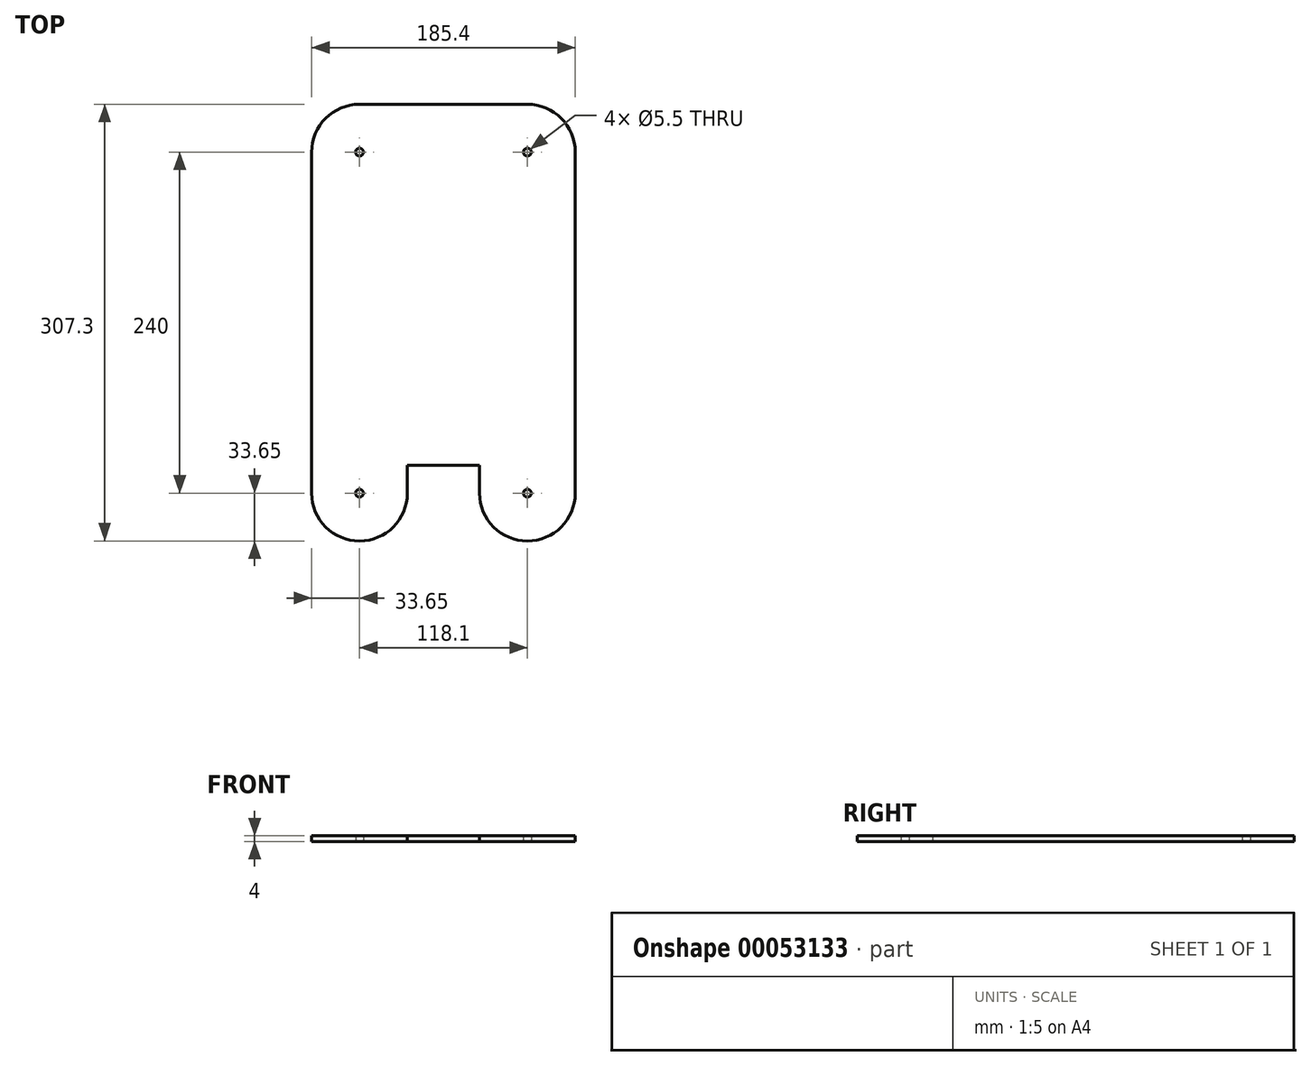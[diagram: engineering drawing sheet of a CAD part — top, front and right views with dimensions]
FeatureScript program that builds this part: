
annotation { "Feature Type Name" : "Feature", "Feature Type Description" : "" }
export const myFeature = defineFeature(function(context is Context, id is Id, definition is map)
    precondition{}
    {
        {
            var Q0;
            Q0=qCreatedBy(makeId("Top.planeOp"),FACE);
            var sketch = newSketch(context, id + "F0", { "sketchPlane" : qUnion([Q0])});
            skLineSegment(sketch, "E0.rect.bottom", {"start": v(61.55, 153.65) * mm, "end": v(-61.55, 153.65) * mm});
            skLineSegment(sketch, "E0.rect.top", {"start": v(61.55, -153.65) * mm, "end": v(-61.55, -153.65) * mm});
            skLineSegment(sketch, "E0.rect.left", {"start": v(92.7, 122.5) * mm, "end": v(92.7, -122.5) * mm});
            skLineSegment(sketch, "E0.rect.right", {"start": v(-92.7, 122.5) * mm, "end": v(-92.7, -122.5) * mm});
            skPoint(sketch, "E0.rect.middle", {"position": v(0, 0) * mm});
            skArc(sketch, "E1", {"start": v(-61.55, 153.65) * mm, "mid": v(-83.58, 144.53) * mm, "end": v(-92.7, 122.5) * mm});
            skPoint(sketch, "E2", {"position": v(-61.55, 153.65) * mm});
            skPoint(sketch, "E3", {"position": v(-92.7, 122.5) * mm});
            skPoint(sketch, "E4", {"position": v(-92.7, 153.65) * mm});
            skPoint(sketch, "E5", {"position": v(92.7, 153.65) * mm});
            skPoint(sketch, "E6", {"position": v(-92.7, -153.65) * mm});
            skPoint(sketch, "E7", {"position": v(92.7, -153.65) * mm});
            skArc(sketch, "E8", {"start": v(92.7, 122.5) * mm, "mid": v(83.58, 144.53) * mm, "end": v(61.55, 153.65) * mm});
            skArc(sketch, "E9", {"start": v(61.55, -153.65) * mm, "mid": v(83.58, -144.53) * mm, "end": v(92.7, -122.5) * mm});
            skArc(sketch, "E10", {"start": v(-92.7, -122.5) * mm, "mid": v(-83.58, -144.53) * mm, "end": v(-61.55, -153.65) * mm});
            skPoint(sketch, "E11", {"position": v(61.55, 153.65) * mm});
            skPoint(sketch, "E12", {"position": v(92.7, 122.5) * mm});
            skPoint(sketch, "E13", {"position": v(92.7, -122.5) * mm});
            skPoint(sketch, "E14", {"position": v(-92.7, -122.5) * mm});
            skPoint(sketch, "E15", {"position": v(61.55, -153.65) * mm});
            skPoint(sketch, "E16", {"position": v(-61.55, -153.65) * mm});
            skPoint(sketch, "E17", {"position": v(-183.97, 39.4) * mm});
            skPoint(sketch, "E18", {"position": v(-61.55, 120) * mm});
            skPoint(sketch, "E19", {"position": v(61.55, 120) * mm});
            skPoint(sketch, "E20", {"position": v(61.55, -120) * mm});
            skPoint(sketch, "E21", {"position": v(-61.55, -120) * mm});
            skPoint(sketch, "E22", {"position": v(59.05, -120) * mm});
            skPoint(sketch, "E23", {"position": v(-59.05, -120) * mm});
            skPoint(sketch, "E24", {"position": v(-59.05, 120) * mm});
            skPoint(sketch, "E25", {"position": v(59.05, 120) * mm});
            skCircle(sketch, "E26", {"center": v(59.05, -120) * mm, "radius": 2.75 * mm});
            skCircle(sketch, "E27", {"center": v(-59.05, -120) * mm, "radius": 2.75 * mm});
            skCircle(sketch, "E28", {"center": v(-59.05, 120) * mm, "radius": 2.75 * mm});
            skCircle(sketch, "E29", {"center": v(59.05, 120) * mm, "radius": 2.75 * mm});
            skSolve(sketch);
        }
        {
            var Q0;
            Q0=qSketchRegion(id+"F0",true);
            extrude(context, id + "F1", {"entities" : qUnion([Q0]), "depth" : 4 * mm});
        }
        {
            var Q0;
            Q0=makeQuery(id+"F1.opExtrude","CAP_FACE",FACE,{"disambiguationData":[OSD([sQuery(id+"F0.wireOp",EDGE,"E0.rect.bottom"),sQuery(id+"F0.wireOp",EDGE,"E0.rect.top"),sQuery(id+"F0.wireOp",EDGE,"E0.rect.left"),sQuery(id+"F0.wireOp",EDGE,"E0.rect.right"),sQuery(id+"F0.wireOp",EDGE,"E1"),sQuery(id+"F0.wireOp",EDGE,"E8"),sQuery(id+"F0.wireOp",EDGE,"E9"),sQuery(id+"F0.wireOp",EDGE,"E10"),sQuery(id+"F0.wireOp",EDGE,"E26"),sQuery(id+"F0.wireOp",EDGE,"E27"),sQuery(id+"F0.wireOp",EDGE,"E28"),sQuery(id+"F0.wireOp",EDGE,"E29")])],"isStart":false});
            var sketch = newSketch(context, id + "F2", { "sketchPlane" : qUnion([Q0])});
            skLineSegment(sketch, "E30.rect.bottom", {"start": v(143.81, 176.18) * mm, "end": v(-143.81, 176.18) * mm});
            skLineSegment(sketch, "E30.rect.top", {"start": v(143.81, -176.18) * mm, "end": v(-143.81, -176.18) * mm});
            skLineSegment(sketch, "E30.rect.left", {"start": v(143.81, 176.18) * mm, "end": v(143.81, -176.18) * mm});
            skLineSegment(sketch, "E30.rect.right", {"start": v(-143.81, 176.18) * mm, "end": v(-143.81, -176.18) * mm});
            skArc(sketch, "E31", {"start": v(-25.4, 120) * mm, "mid": v(-59.05, 153.65) * mm, "end": v(-92.7, 120) * mm});
            skArc(sketch, "E32", {"start": v(92.7, 120) * mm, "mid": v(59.05, 153.65) * mm, "end": v(25.4, 120) * mm});
            skArc(sketch, "E33", {"start": v(-92.7, -120) * mm, "mid": v(-59.05, -153.65) * mm, "end": v(-25.4, -120) * mm});
            skArc(sketch, "E34", {"start": v(25.4, -120) * mm, "mid": v(59.05, -153.65) * mm, "end": v(92.7, -120) * mm});
            skLineSegment(sketch, "E35", {"start": v(-92.7, -120) * mm, "end": v(-92.7, 122.5) * mm});
            skLineSegment(sketch, "E36", {"start": v(92.7, 122.5) * mm, "end": v(92.7, -120) * mm});
            skPoint(sketch, "E37.start.orphan", {"position": v(-92.7, 120) * mm});
            skLineSegment(sketch, "E38", {"start": v(-59.05, -153.65) * mm, "end": v(59.05, -153.65) * mm});
            skLineSegment(sketch, "E39", {"start": v(-59.05, 153.65) * mm, "end": v(59.05, 153.65) * mm});
            skSolve(sketch);
        }
        {
            var Q0;
            Q0=qSketchRegion(id+"F2",true);
            extrude(context, id + "F3", {"entities" : qUnion([Q0]), "operationType" : NewBodyOperationType.REMOVE, "oppositeDirection" : true, "depth" : 25 * mm});
        }
        {
            var Q0;
            Q0=makeQuery(id+"F1.opExtrude","CAP_FACE",FACE,{"disambiguationData":[OSD([sQuery(id+"F0.wireOp",EDGE,"E0.rect.bottom"),sQuery(id+"F0.wireOp",EDGE,"E0.rect.top"),sQuery(id+"F0.wireOp",EDGE,"E0.rect.left"),sQuery(id+"F0.wireOp",EDGE,"E0.rect.right"),sQuery(id+"F0.wireOp",EDGE,"E1"),sQuery(id+"F0.wireOp",EDGE,"E8"),sQuery(id+"F0.wireOp",EDGE,"E9"),sQuery(id+"F0.wireOp",EDGE,"E10"),sQuery(id+"F0.wireOp",EDGE,"E26"),sQuery(id+"F0.wireOp",EDGE,"E27"),sQuery(id+"F0.wireOp",EDGE,"E28"),sQuery(id+"F0.wireOp",EDGE,"E29")])],"isStart":false});
            var sketch = newSketch(context, id + "F4", { "sketchPlane" : qUnion([Q0])});
            skArc(sketch, "E40", {"start": v(25.4, -120) * mm, "mid": v(35.26, -143.8) * mm, "end": v(59.05, -153.65) * mm});
            skArc(sketch, "E41", {"start": v(-59.05, -153.65) * mm, "mid": v(-35.26, -143.8) * mm, "end": v(-25.4, -120) * mm});
            skLineSegment(sketch, "E42", {"start": v(0, 153.65) * mm, "end": v(0, -100.35) * mm});
            skPoint(sketch, "E42.endSnap0", {"position": v(0, 153.65) * mm});
            skLineSegment(sketch, "E43", {"start": v(-25.4, -100.35) * mm, "end": v(25.4, -100.35) * mm});
            skPoint(sketch, "E44", {"position": v(-59.05, -153.65) * mm});
            skPoint(sketch, "E45", {"position": v(59.05, -153.65) * mm});
            skLineSegment(sketch, "E46", {"start": v(-59.05, -153.65) * mm, "end": v(59.05, -153.65) * mm});
            skPoint(sketch, "E47", {"position": v(25.4, -120) * mm});
            skPoint(sketch, "E48", {"position": v(-25.4, -120) * mm});
            skLineSegment(sketch, "E49", {"start": v(-25.4, -120) * mm, "end": v(-25.4, -100.35) * mm});
            skLineSegment(sketch, "E50", {"start": v(25.4, -120) * mm, "end": v(25.4, -100.35) * mm});
            skPoint(sketch, "E51.orphan", {"position": v(-31.73, -100.35) * mm});
            skSolve(sketch);
        }
        {
            var Q0;
            Q0 = qSketchRegion(id + "F4", true);
            extrude(context, id + "F5", {"entities" : qUnion([Q0]), "operationType" : NewBodyOperationType.REMOVE, "oppositeDirection" : true, "depth" : 25 * mm});
        }
    });
